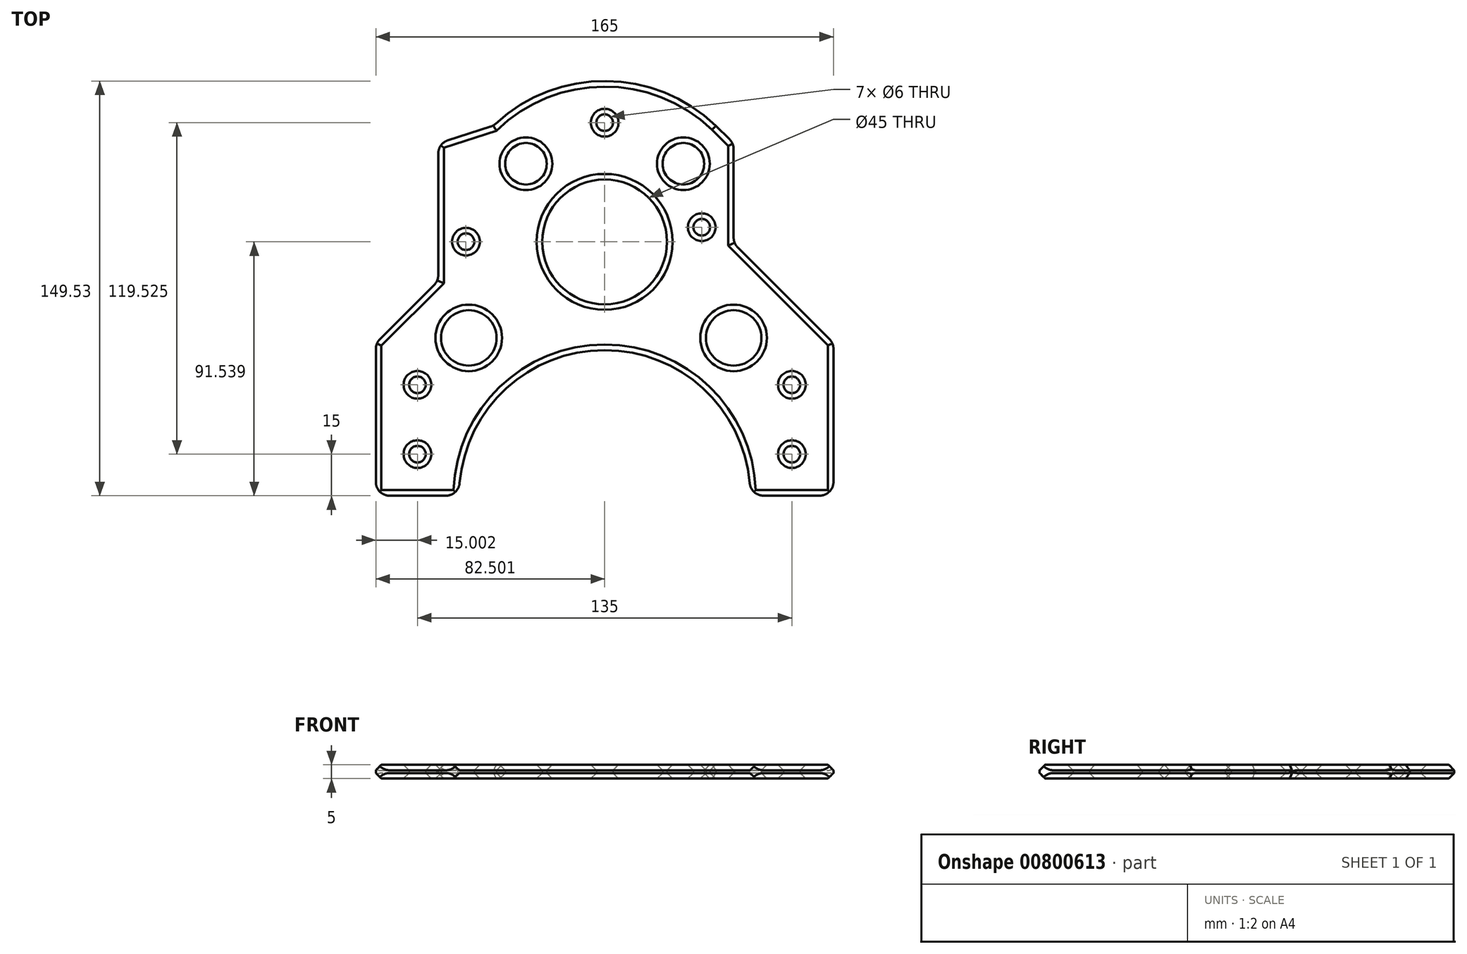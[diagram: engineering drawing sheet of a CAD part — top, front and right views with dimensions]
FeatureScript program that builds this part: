
annotation { "Feature Type Name" : "Feature", "Feature Type Description" : "" }
export const myFeature = defineFeature(function(context is Context, id is Id, definition is map)
    precondition{}
    {
        {
            var Q0;
            Q0=qCreatedBy(makeId("Top.planeOp"),FACE);
            var sketch = newSketch(context, id + "F0", { "sketchPlane" : qUnion([Q0])});
            skArc(sketch, "E0", {"start": v(92.61, -67.9) * mm, "mid": v(40.1, -15.4) * mm, "end": v(-12.39, -67.92) * mm});
            skLineSegment(sketch, "E1", {"start": v(122.61, -67.9) * mm, "end": v(122.61, -12.9) * mm});
            skLineSegment(sketch, "E2", {"start": v(122.61, -12.9) * mm, "end": v(86.61, -12.9) * mm});
            skLineSegment(sketch, "E3", {"start": v(86.61, -12.9) * mm, "end": v(86.61, 59.1) * mm});
            skLineSegment(sketch, "E4", {"start": v(-19.89, 59.1) * mm, "end": v(-19.89, -12.92) * mm});
            skLineSegment(sketch, "E5", {"start": v(-19.89, -12.92) * mm, "end": v(-42.39, -12.92) * mm});
            skLineSegment(sketch, "E6", {"start": v(-42.39, -12.92) * mm, "end": v(-42.39, -67.92) * mm});
            skLineSegment(sketch, "E7", {"start": v(-42.39, -67.92) * mm, "end": v(-12.39, -67.92) * mm});
            skLineSegment(sketch, "E8", {"start": v(92.61, -67.9) * mm, "end": v(122.61, -67.9) * mm});
            skArc(sketch, "E9", {"start": v(80.22, 65.5) * mm, "mid": v(40.11, 81.6) * mm, "end": v(0, 65.5) * mm});
            skCircle(sketch, "E10", {"center": v(40.11, 66.6) * mm, "radius": 3 * mm});
            skCircle(sketch, "E11", {"center": v(75.11, 28.9) * mm, "radius": 3 * mm});
            skCircle(sketch, "E12", {"center": v(-9.89, 23.7) * mm, "radius": 3 * mm});
            skCircle(sketch, "E13", {"center": v(-27.39, -27.92) * mm, "radius": 3 * mm});
            skCircle(sketch, "E14", {"center": v(-27.39, -52.92) * mm, "radius": 3 * mm});
            skCircle(sketch, "E15", {"center": v(107.61, -27.92) * mm, "radius": 3 * mm});
            skCircle(sketch, "E16", {"center": v(107.61, -52.92) * mm, "radius": 3 * mm});
            skLineSegment(sketch, "E17", {"start": v(80.22, 65.5) * mm, "end": v(86.61, 59.1) * mm});
            skLineSegment(sketch, "E18", {"start": v(0, 65.5) * mm, "end": v(-19.89, 59.1) * mm});
            skLineSegment(sketch, "E19", {"start": v(40.11, 81.6) * mm, "end": v(40.11, -15.4) * mm});
            skLineSegment(sketch, "E20", {"start": v(122.61, -12.9) * mm, "end": v(86.61, 23.1) * mm});
            skLineSegment(sketch, "E21", {"start": v(-42.39, -12.92) * mm, "end": v(-19.89, 9.58) * mm});
            skCircle(sketch, "E22", {"center": v(40.11, 23.62) * mm, "radius": 22.5 * mm});
            skCircle(sketch, "E23", {"center": v(11.72, 51.8) * mm, "radius": 7.5 * mm});
            skCircle(sketch, "E24", {"center": v(68.5, 51.8) * mm, "radius": 7.5 * mm});
            skCircle(sketch, "E25", {"center": v(86.61, -11) * mm, "radius": 10 * mm});
            skCircle(sketch, "E26", {"center": v(-8.89, -11) * mm, "radius": 10 * mm});
            skSolve(sketch);
        }
        {
            var Q0;
            Q0=qSketchRegion(id+"F0",true);
            extrude(context, id + "F1", {"entities" : qUnion([Q0]), "depth" : 5 * mm, "offsetDistance" : 25 * mm});
        }
        {
            var Q0;
            Q0=makeQuery(id+"F1.opExtrude","CAP_FACE",FACE,{"disambiguationData":[OSD([sQuery(id+"F0.wireOp",EDGE,"E0"),sQuery(id+"F0.wireOp",EDGE,"E1"),sQuery(id+"F0.wireOp",EDGE,"E3"),sQuery(id+"F0.wireOp",EDGE,"E4"),sQuery(id+"F0.wireOp",EDGE,"E6"),sQuery(id+"F0.wireOp",EDGE,"E7"),sQuery(id+"F0.wireOp",EDGE,"E8"),sQuery(id+"F0.wireOp",EDGE,"E9"),sQuery(id+"F0.wireOp",EDGE,"E10"),sQuery(id+"F0.wireOp",EDGE,"E11"),sQuery(id+"F0.wireOp",EDGE,"E12"),sQuery(id+"F0.wireOp",EDGE,"E13"),sQuery(id+"F0.wireOp",EDGE,"E14"),sQuery(id+"F0.wireOp",EDGE,"E15"),sQuery(id+"F0.wireOp",EDGE,"E16"),sQuery(id+"F0.wireOp",EDGE,"E17"),sQuery(id+"F0.wireOp",EDGE,"E18"),sQuery(id+"F0.wireOp",EDGE,"E20"),sQuery(id+"F0.wireOp",EDGE,"E21")])],"isStart":false});
            var Q1;
            Q1=makeQuery(id+"F1.opExtrude","CAP_FACE",FACE,{"disambiguationData":[OSD([sQuery(id+"F0.wireOp",EDGE,"E0"),sQuery(id+"F0.wireOp",EDGE,"E1"),sQuery(id+"F0.wireOp",EDGE,"E3"),sQuery(id+"F0.wireOp",EDGE,"E4"),sQuery(id+"F0.wireOp",EDGE,"E6"),sQuery(id+"F0.wireOp",EDGE,"E7"),sQuery(id+"F0.wireOp",EDGE,"E8"),sQuery(id+"F0.wireOp",EDGE,"E9"),sQuery(id+"F0.wireOp",EDGE,"E10"),sQuery(id+"F0.wireOp",EDGE,"E11"),sQuery(id+"F0.wireOp",EDGE,"E12"),sQuery(id+"F0.wireOp",EDGE,"E13"),sQuery(id+"F0.wireOp",EDGE,"E14"),sQuery(id+"F0.wireOp",EDGE,"E15"),sQuery(id+"F0.wireOp",EDGE,"E16"),sQuery(id+"F0.wireOp",EDGE,"E17"),sQuery(id+"F0.wireOp",EDGE,"E18"),sQuery(id+"F0.wireOp",EDGE,"E20"),sQuery(id+"F0.wireOp",EDGE,"E21")])],"isStart":true});
            chamfer(context, id + "F2", {"entities" : qUnion([Q0, Q1]), "width" : 2 * mm, "tangentPropagation" : true});
        }
        {
            var Q0;
            Q0=makeQuery(id+"F1.opExtrude","SWEPT_EDGE",EDGE,{"disambiguationData":[OSD([sQuery(id+"F0.wireOp",EDGE,"E0"),sQuery(id+"F0.wireOp",EDGE,"E7")])]});
            var Q1;
            Q1=makeQuery(id+"F1.opExtrude","SWEPT_EDGE",EDGE,{"disambiguationData":[OSD([sQuery(id+"F0.wireOp",EDGE,"E6"),sQuery(id+"F0.wireOp",EDGE,"E7")])]});
            var Q2;
            Q2=makeQuery(id+"F1.opExtrude","SWEPT_EDGE",EDGE,{"disambiguationData":[OSD([sQuery(id+"F0.wireOp",EDGE,"E0"),sQuery(id+"F0.wireOp",EDGE,"E8")])]});
            var Q3;
            Q3=makeQuery(id+"F1.opExtrude","SWEPT_EDGE",EDGE,{"disambiguationData":[OSD([sQuery(id+"F0.wireOp",EDGE,"E1"),sQuery(id+"F0.wireOp",EDGE,"E8")])]});
            var Q4;
            Q4=makeQuery(id+"F1.opExtrude","SWEPT_EDGE",EDGE,{"disambiguationData":[OSD([sQuery(id+"F0.wireOp",EDGE,"E1"),sQuery(id+"F0.wireOp",EDGE,"E2"),sQuery(id+"F0.wireOp",EDGE,"E20")])]});
            var Q5;
            Q5=makeQuery(id+"F1.opExtrude","SWEPT_EDGE",EDGE,{"disambiguationData":[OSD([sQuery(id+"F0.wireOp",EDGE,"E5"),sQuery(id+"F0.wireOp",EDGE,"E6"),sQuery(id+"F0.wireOp",EDGE,"E21")])]});
            var Q6;
            Q6=makeQuery(id+"F1.opExtrude","SWEPT_EDGE",EDGE,{"disambiguationData":[OSD([sQuery(id+"F0.wireOp",EDGE,"E4"),sQuery(id+"F0.wireOp",EDGE,"E21")])]});
            var Q7;
            Q7=makeQuery(id+"F1.opExtrude","SWEPT_EDGE",EDGE,{"disambiguationData":[OSD([sQuery(id+"F0.wireOp",EDGE,"E4"),sQuery(id+"F0.wireOp",EDGE,"E18")])]});
            var Q8;
            Q8=makeQuery(id+"F1.opExtrude","SWEPT_EDGE",EDGE,{"disambiguationData":[OSD([sQuery(id+"F0.wireOp",EDGE,"E9"),sQuery(id+"F0.wireOp",EDGE,"E18")])]});
            var Q9;
            Q9=makeQuery(id+"F1.opExtrude","SWEPT_EDGE",EDGE,{"disambiguationData":[OSD([sQuery(id+"F0.wireOp",EDGE,"E3"),sQuery(id+"F0.wireOp",EDGE,"E17")])]});
            var Q10;
            Q10=makeQuery(id+"F1.opExtrude","SWEPT_EDGE",EDGE,{"disambiguationData":[OSD([sQuery(id+"F0.wireOp",EDGE,"E3"),sQuery(id+"F0.wireOp",EDGE,"E20")])]});
            fillet(context, id + "F3", {"entities" : qUnion([Q0, Q1, Q2, Q3, Q4, Q5, Q6, Q7, Q8, Q9, Q10]), "radius" : 5 * mm, "tangentPropagation" : true, "allowEdgeOverflow" : false});
        }
    });
